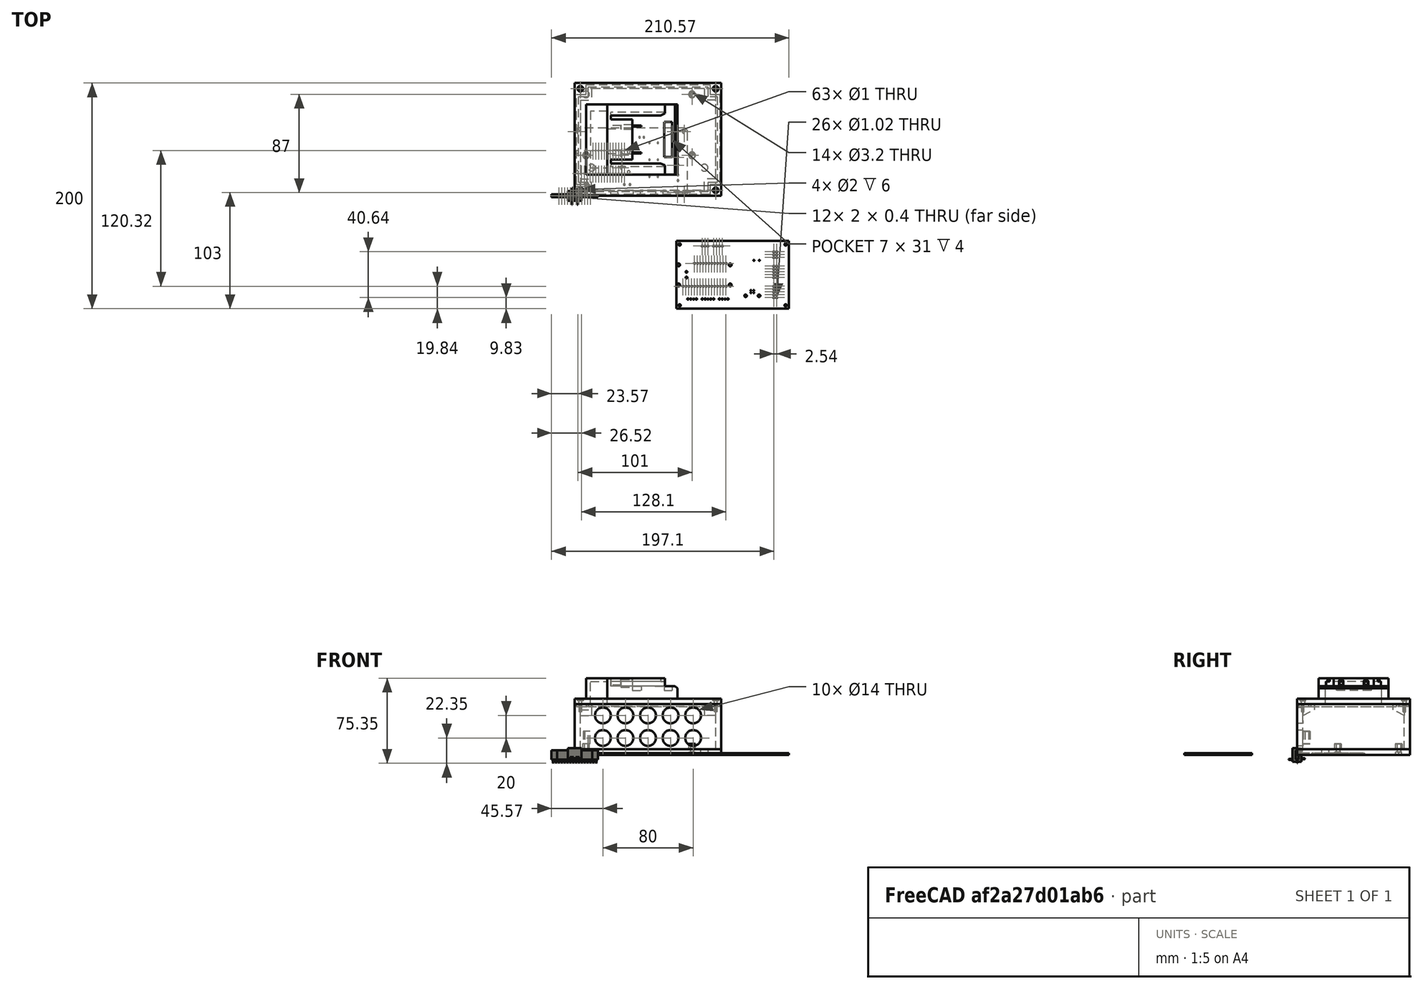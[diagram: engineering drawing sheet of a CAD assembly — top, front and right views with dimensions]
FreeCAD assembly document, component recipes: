
FREECAD ASSEMBLY — COMPONENT RECIPES ("case")

This assembly document has 7 components, labeled P0..P6 below (a component is one placed body or linked part). 5 of them carry a construction recipe — the FreeCAD feature program that regenerates the part from scratch, quoted from this document or its linked companion documents; the rest are supplied as boundary geometry only. No exploded tour is included for this assembly.
COMPONENT P0 — recipe-attached ("middle", modeled in this document).
Construction recipe (the document's own serialized feature program — sketch geometry with constraints, then the solid features built on it; lengths are millimeters unless a unit is written):

FEATURE [Sketcher::SketchObject] Sketch
  MapMode = 5
  Support = -> [XY_Plane]
  sketch-geometry (8):
    g0: LineSegment StartX=0 StartY=0 StartZ=0 EndX=130 EndY=0 EndZ=0
    g1: LineSegment StartX=130 StartY=0 StartZ=0 EndX=130 EndY=100 EndZ=0
    g2: LineSegment StartX=130 StartY=100 StartZ=0 EndX=0 EndY=100 EndZ=0
    g3: LineSegment StartX=0 StartY=100 StartZ=0 EndX=0 EndY=0 EndZ=0
    g4: LineSegment StartX=5 StartY=5 StartZ=0 EndX=125 EndY=5 EndZ=0
    g5: LineSegment StartX=125 StartY=5 StartZ=0 EndX=125 EndY=95 EndZ=0
    g6: LineSegment StartX=125 StartY=95 StartZ=0 EndX=5 EndY=95 EndZ=0
    g7: LineSegment StartX=5 StartY=95 StartZ=0 EndX=5 EndY=5 EndZ=0
  constraints (21):
    c: Coincident(g0,g1)
    c: Coincident(g1,g2)
    c: Coincident(g2,g3)
    c: Coincident(g3,g0)
    c: Horizontal(g0)
    c: Horizontal(g2)
    c: Vertical(g1)
    c: Vertical(g3)
    c: Coincident(g-1,g0)
    c: DistanceX(g2,g2) = 130
    c: DistanceY(g1,g1) = 100
    c: Coincident(g4,g5)
    c: Coincident(g5,g6)
    c: Coincident(g6,g7)
    c: Coincident(g7,g4)
    c: Horizontal(g4)
    c: Horizontal(g6)
    c: Vertical(g5)
    c: Vertical(g7)
    c: DistanceX(g6,g6) = 120
    c: DistanceY(g5,g5) = 90
FEATURE [PartDesign::Pad] Pad
  AllowMultiFace = false
  Length = 40
  Length2 = 100
  Profile = -> Sketch
  Type = 0
FEATURE [Sketcher::SketchObject] Sketch004
  MapMode = 5
  Placement = pos=(5,0,0) rot=(0.57735,0.57735,0.57735;2.0944rad)
  Support = -> [Pad]
  sketch-geometry (8):
    g0: LineSegment StartX=5 StartY=40 StartZ=0 EndX=15 EndY=40 EndZ=0
    g1: LineSegment StartX=15 StartY=40 StartZ=0 EndX=15 EndY=35 EndZ=0
    g2: LineSegment StartX=15 StartY=35 StartZ=0 EndX=5 EndY=35 EndZ=0
    g3: LineSegment StartX=5 StartY=35 StartZ=0 EndX=5 EndY=40 EndZ=0
    g4: LineSegment StartX=85 StartY=40 StartZ=0 EndX=95 EndY=40 EndZ=0
    g5: LineSegment StartX=95 StartY=40 StartZ=0 EndX=95 EndY=35 EndZ=0
    g6: LineSegment StartX=95 StartY=35 StartZ=0 EndX=85 EndY=35 EndZ=0
    g7: LineSegment StartX=85 StartY=35 StartZ=0 EndX=85 EndY=40 EndZ=0
  constraints (21):
    c: Coincident(g0,g1)
    c: Coincident(g1,g2)
    c: Coincident(g2,g3)
    c: Coincident(g3,g0)
    c: Horizontal(g0)
    c: Horizontal(g2)
    c: Vertical(g1)
    c: Vertical(g3)
    c: Coincident(g4,g5)
    c: Coincident(g5,g6)
    c: Coincident(g6,g7)
    c: Coincident(g7,g4)
    c: Horizontal(g4)
    c: Horizontal(g6)
    c: Vertical(g5)
    c: Vertical(g7)
    c: Equal(g4,g0)
    c: Equal(g1,g5)
    c: DistanceY(g3,g3) = 5
    c: DistanceX(g0,g4) = 70
    c: DistanceX(g0,g0) = 10
FEATURE [PartDesign::Pad] Pad003
  AllowMultiFace = false
  BaseFeature = -> Pad
  Length = 10
  Length2 = 100
  Profile = -> Sketch004
  Type = 0
FEATURE [Sketcher::SketchObject] Sketch005
  MapMode = 5
  Placement = pos=(125,0,0) rot=(0.57735,-0.57735,-0.57735;2.0944rad)
  Support = -> [Pad003]
  sketch-geometry (8):
    g0: LineSegment StartX=-95 StartY=40 StartZ=0 EndX=-85 EndY=40 EndZ=0
    g1: LineSegment StartX=-85 StartY=40 StartZ=0 EndX=-85 EndY=35 EndZ=0
    g2: LineSegment StartX=-85 StartY=35 StartZ=0 EndX=-95 EndY=35 EndZ=0
    g3: LineSegment StartX=-95 StartY=35 StartZ=0 EndX=-95 EndY=40 EndZ=0
    g4: LineSegment StartX=-15 StartY=40 StartZ=0 EndX=-5 EndY=40 EndZ=0
    g5: LineSegment StartX=-5 StartY=40 StartZ=0 EndX=-5 EndY=35 EndZ=0
    g6: LineSegment StartX=-5 StartY=35 StartZ=0 EndX=-15 EndY=35 EndZ=0
    g7: LineSegment StartX=-15 StartY=35 StartZ=0 EndX=-15 EndY=40 EndZ=0
  constraints (21):
    c: Coincident(g0,g1)
    c: Coincident(g1,g2)
    c: Coincident(g2,g3)
    c: Coincident(g3,g0)
    c: Horizontal(g0)
    c: Horizontal(g2)
    c: Vertical(g1)
    c: Vertical(g3)
    c: Coincident(g4,g5)
    c: Coincident(g5,g6)
    c: Coincident(g6,g7)
    c: Coincident(g7,g4)
    c: Horizontal(g4)
    c: Horizontal(g6)
    c: Vertical(g5)
    c: Vertical(g7)
    c: Equal(g0,g4)
    c: Equal(g7,g1)
    c: DistanceX(g0,g0) = 10
    c: DistanceY(g1,g1) = 5
    c: DistanceX(g0,g4) = 70
FEATURE [PartDesign::Pad] Pad004
  AllowMultiFace = false
  BaseFeature = -> Pad003
  Length = 10
  Length2 = 100
  Profile = -> Sketch005
  Type = 0
FEATURE [Sketcher::SketchObject] Sketch006
  MapMode = 5
  Placement = pos=(5,0,0) rot=(0.57735,0.57735,0.57735;2.0944rad)
  Support = -> [Pad004]
  sketch-geometry (6):
    g0: LineSegment StartX=5 StartY=30 StartZ=0 EndX=5 EndY=35 EndZ=0
    g1: LineSegment StartX=5 StartY=35 StartZ=0 EndX=15 EndY=35 EndZ=0
    g2: LineSegment StartX=85 StartY=35 StartZ=0 EndX=95 EndY=35 EndZ=0
    g3: LineSegment StartX=95 StartY=35 StartZ=0 EndX=95 EndY=30 EndZ=0
    g4: LineSegment StartX=95 StartY=30 StartZ=0 EndX=85 EndY=35 EndZ=0
    g5: LineSegment StartX=5 StartY=30 StartZ=0 EndX=15 EndY=35 EndZ=0
  constraints (13):
    c: Coincident(g0,g1)
    c: Coincident(g2,g3)
    c: Coincident(g3,g4)
    c: Horizontal(g2)
    c: Horizontal(g1)
    c: Vertical(g0)
    c: Vertical(g3)
    c: Coincident(g5,g1)
    c: Equal(g2,g1)
    c: Equal(g0,g3)
    c: DistanceX(g1,g1) = 10
    c: DistanceX(g1,g2) = 70
    c: DistanceY(g0,g0) = 5
FEATURE [PartDesign::Pad] Pad005
  AllowMultiFace = false
  BaseFeature = -> Pad004
  Length = 10
  Length2 = 100
  Profile = -> Sketch006
  Type = 0
FEATURE [Sketcher::SketchObject] Sketch007
  MapMode = 5
  Placement = pos=(125,0,0) rot=(0.57735,-0.57735,-0.57735;2.0944rad)
  Support = -> [Pad005]
  sketch-geometry (7):
    g0: LineSegment StartX=0 StartY=35 StartZ=0 EndX=-5 EndY=35 EndZ=0
    g1: LineSegment StartX=-5 StartY=35 StartZ=0 EndX=-5 EndY=30 EndZ=0
    g2: LineSegment StartX=-5 StartY=30 StartZ=0 EndX=-15 EndY=35 EndZ=0
    g3: LineSegment StartX=-85 StartY=35 StartZ=0 EndX=-95 EndY=35 EndZ=0
    g4: LineSegment StartX=-95 StartY=35 StartZ=0 EndX=-95 EndY=30 EndZ=0
    g5: LineSegment StartX=-95 StartY=30 StartZ=0 EndX=-85 EndY=35 EndZ=0
    g6: LineSegment StartX=-15 StartY=35 StartZ=0 EndX=-5 EndY=35 EndZ=0
  constraints (18):
    c: Coincident(g0,g1)
    c: Coincident(g1,g2)
    c: Coincident(g3,g4)
    c: Coincident(g4,g5)
    c: Coincident(g6,g0)
    c: Coincident(g2,g6)
    c: Vertical(g1)
    c: Vertical(g4)
    c: Horizontal(g6)
    c: Horizontal(g3)
    c: Horizontal(g0)
    c: Equal(g6,g3)
    c: Equal(g4,g1)
    c: DistanceY(g-1,g0) = 35
    c: DistanceY(g1,g1) = 5
    c: DistanceX(g0,g0) = 5
    c: DistanceX(g6,g6) = 10
    c: DistanceX(g3,g2) = 70
FEATURE [PartDesign::Pad] Pad006
  AllowMultiFace = false
  BaseFeature = -> Pad005
  Length = 10
  Length2 = 100
  Profile = -> Sketch007
  Type = 0
FEATURE [Sketcher::SketchObject] Sketch009
  MapMode = 5
  Placement = pos=(0,0,40) rot=(0,0,1;0rad)
  sketch-geometry (4):
    g0: Circle CenterX=5 CenterY=95 CenterZ=0 NormalX=0 NormalY=0 NormalZ=1 AngleXU=0 Radius=1
    g1: Circle CenterX=125 CenterY=95 CenterZ=0 NormalX=0 NormalY=0 NormalZ=1 AngleXU=0 Radius=1
    g2: Circle CenterX=125 CenterY=5 CenterZ=0 NormalX=0 NormalY=0 NormalZ=1 AngleXU=0 Radius=1
    g3: Circle CenterX=5 CenterY=5 CenterZ=0 NormalX=0 NormalY=0 NormalZ=1 AngleXU=0 Radius=1
  constraints (6):
    c: DistanceY(g3,g0) = 90
    c: DistanceX(g0,g1) = 120
    c: Equal(g0,g1)
    c: Equal(g0,g2)
    c: Equal(g0,g3)
    c: Radius(g0) = 1
FEATURE [PartDesign::Pocket] Pocket002
  AllowMultiFace = false
  BaseFeature = -> Pad006
  Length = 7
  Length2 = 100
  Profile = -> Sketch009
  Type = 0
FEATURE [Sketcher::SketchObject] Sketch011
  MapMode = 5
  Placement = pos=(0,0,0) rot=(1,0,0;1.5708rad)
  sketch-geometry (10):
    g0: Circle CenterX=25 CenterY=30 CenterZ=0 NormalX=0 NormalY=0 NormalZ=1 AngleXU=0 Radius=7
    g1: Circle CenterX=45 CenterY=30 CenterZ=0 NormalX=0 NormalY=0 NormalZ=1 AngleXU=0 Radius=7
    g2: Circle CenterX=45 CenterY=10 CenterZ=0 NormalX=0 NormalY=0 NormalZ=1 AngleXU=0 Radius=7
    g3: Circle CenterX=25 CenterY=10 CenterZ=0 NormalX=0 NormalY=0 NormalZ=1 AngleXU=0 Radius=7
    g4: Circle CenterX=65 CenterY=30 CenterZ=0 NormalX=0 NormalY=0 NormalZ=1 AngleXU=0 Radius=7
    g5: Circle CenterX=85 CenterY=30 CenterZ=0 NormalX=0 NormalY=0 NormalZ=1 AngleXU=0 Radius=7
    g6: Circle CenterX=85 CenterY=10 CenterZ=0 NormalX=0 NormalY=0 NormalZ=1 AngleXU=0 Radius=7
    g7: Circle CenterX=65 CenterY=10 CenterZ=0 NormalX=0 NormalY=0 NormalZ=1 AngleXU=0 Radius=7
    g8: Circle CenterX=105 CenterY=10 CenterZ=0 NormalX=0 NormalY=0 NormalZ=1 AngleXU=0 Radius=7
    g9: Circle CenterX=105 CenterY=30 CenterZ=0 NormalX=0 NormalY=0 NormalZ=1 AngleXU=0 Radius=7
  constraints (12):
    c: Equal(g0,g1)
    c: Equal(g1,g2)
    c: Equal(g2,g3)
    c: Equal(g4,g5)
    c: Equal(g3,g7)
    c: Equal(g2,g6)
    c: Equal(g1,g5)
    c: Radius(g0) = 7
    c: DistanceX(g0,g1) = 20
    c: DistanceY(g6,g5) = 20
    c: Equal(g6,g8)
    c: Equal(g9,g8)
FEATURE [PartDesign::Pocket] Pocket004
  AllowMultiFace = false
  BaseFeature = -> Pocket002
  Length = 5
  Length2 = 100
  Profile = -> Sketch011
  Type = 0
FEATURE [PartDesign::Pocket] Pocket007
  AllowMultiFace = false
  BaseFeature = -> Pocket004
  Length = 1
  Length2 = 100
  Profile = -> Sketch009
  Type = 0
FEATURE [Sketcher::SketchObject] Sketch014
  MapMode = 5
  Placement = pos=(0,0,40) rot=(0,0,1;0rad)
  Support = -> [Pocket004]
  sketch-geometry (25):
    g0: LineSegment StartX=12 StartY=88 StartZ=0 EndX=12 EndY=96.5 EndZ=0
    g1: LineSegment StartX=12 StartY=96.5 StartZ=0 EndX=118 EndY=96.5 EndZ=0
    g2: LineSegment StartX=118 StartY=96.5 StartZ=0 EndX=118 EndY=88 EndZ=0
    g3: LineSegment StartX=118 StartY=88 StartZ=0 EndX=126.5 EndY=88 EndZ=0
    g4: LineSegment StartX=126.5 StartY=88 StartZ=0 EndX=126.5 EndY=12 EndZ=0
    g5: LineSegment StartX=126.5 StartY=12 StartZ=0 EndX=118 EndY=12 EndZ=0
    g6: LineSegment StartX=118 StartY=12 StartZ=0 EndX=118 EndY=3.5 EndZ=0
    g7: LineSegment StartX=118 StartY=3.5 StartZ=0 EndX=12 EndY=3.5 EndZ=0
    g8: LineSegment StartX=12 StartY=3.5 StartZ=0 EndX=12 EndY=12 EndZ=0
    g9: LineSegment StartX=12 StartY=12 StartZ=0 EndX=3.5 EndY=12 EndZ=0
    g10: LineSegment StartX=3.5 StartY=12 StartZ=0 EndX=3.5 EndY=88 EndZ=0
    g11: LineSegment StartX=3.5 StartY=88 StartZ=0 EndX=12 EndY=88 EndZ=0
    g12: LineSegment StartX=1.5 StartY=10 StartZ=0 EndX=1.5 EndY=90 EndZ=0
    g13: LineSegment StartX=1.5 StartY=90 StartZ=0 EndX=10 EndY=90 EndZ=0
    g14: LineSegment StartX=10 StartY=90 StartZ=0 EndX=10 EndY=98.5 EndZ=0
    g15: LineSegment StartX=10 StartY=98.5 StartZ=0 EndX=120 EndY=98.5 EndZ=0
    g16: LineSegment StartX=120 StartY=98.5 StartZ=0 EndX=120 EndY=90 EndZ=0
    g17: LineSegment StartX=120 StartY=90 StartZ=0 EndX=128.5 EndY=90 EndZ=0
    g18: LineSegment StartX=128.5 StartY=90 StartZ=0 EndX=128.5 EndY=10 EndZ=0
    g19: LineSegment StartX=128.5 StartY=10 StartZ=0 EndX=120 EndY=10 EndZ=0
    g20: LineSegment StartX=120 StartY=10 StartZ=0 EndX=120 EndY=1.5 EndZ=0
    g21: LineSegment StartX=120 StartY=1.5 StartZ=0 EndX=10 EndY=1.5 EndZ=0
    g22: LineSegment StartX=10 StartY=1.5 StartZ=0 EndX=10 EndY=10 EndZ=0
    g23: LineSegment StartX=10 StartY=10 StartZ=0 EndX=1.5 EndY=10 EndZ=0
    g24: LineSegment StartX=120 StartY=88 StartZ=0 EndX=118 EndY=88 EndZ=0
  constraints (72):
    c: Coincident(g0,g1)
    c: Coincident(g1,g2)
    c: Coincident(g2,g3)
    c: Coincident(g3,g4)
    c: Coincident(g4,g5)
    c: Coincident(g5,g6)
    c: Coincident(g6,g7)
    c: Coincident(g7,g8)
    c: Coincident(g8,g9)
    c: Coincident(g9,g10)
    c: Coincident(g10,g11)
    c: Coincident(g11,g0)
    c: Vertical(g0)
    c: Vertical(g10)
    c: Vertical(g8)
    c: Vertical(g6)
    c: Vertical(g4)
    c: Horizontal(g1)
    c: Horizontal(g3)
    c: Horizontal(g5)
    c: Horizontal(g7)
    c: Horizontal(g9)
    c: Equal(g1,g7)
    c: Equal(g10,g4)
    c: Equal(g5,g6)
    c: Equal(g3,g2)
    c: Equal(g3,g5)
    c: Equal(g9,g8)
    c: Equal(g0,g11)
    c: Equal(g11,g9)
    c: Equal(g2,g0)
    c: Coincident(g12,g13)
    c: Coincident(g13,g14)
    c: Coincident(g14,g15)
    c: Coincident(g15,g16)
    c: Coincident(g16,g17)
    c: Coincident(g17,g18)
    c: Coincident(g18,g19)
    c: Coincident(g19,g20)
    c: Coincident(g20,g21)
    c: Coincident(g21,g22)
    c: Coincident(g22,g23)
    c: Coincident(g23,g12)
    c: Horizontal(g15)
    c: Horizontal(g21)
    c: Horizontal(g19)
    c: Horizontal(g17)
    c: Horizontal(g13)
    c: Vertical(g12)
    c: Vertical(g22)
    c: Vertical(g20)
    c: Vertical(g18)
    c: Vertical(g16)
    c: Equal(g15,g21)
    c: Equal(g18,g12)
    c: Equal(g22,g20)
    c: Equal(g19,g23)
    c: Equal(g20,g19)
    c: Equal(g17,g16)
    c: Equal(g17,g19)
    c: Equal(g14,g13)
    c: Equal(g14,g16)
    c: Equal(g22,g19)
    c: DistanceY(g12,g12) = 80
    c: DistanceX(g13,g13) = 8.5
    c: DistanceX(g21,g21) = 110
    c: Horizontal(g24)
    c: DistanceY(g24,g16) = 2
    c: DistanceX(g24,g24) = 2
    c: Coincident(g2,g24)
    c: DistanceX(g7,g7) = 106
    c: DistanceY(g4,g4) = 76
FEATURE [PartDesign::Pocket] Pocket008
  AllowMultiFace = false
  BaseFeature = -> Pocket007
  Length = 2
  Length2 = 100
  Profile = -> Sketch014
  Type = 0
FEATURE [PartDesign::Body] Body  label="middle"
  Group = -> [Sketch,Pad,Sketch004,Pad003,Sketch005,Pad004,Sketch006,Pad005,Sketch007,Pad006,Sketch009,Pocket002,Sketch011,Pocket004,Pocket007,Sketch014,Pocket008]
  Origin = -> Origin
  Placement = pos=(0,0,5) rot=(0,0,1;0rad)
  Tip = -> Pocket008
COMPONENT P1 — recipe-attached ("bottom", modeled in this document).
Construction recipe (the document's own serialized feature program — sketch geometry with constraints, then the solid features built on it; lengths are millimeters unless a unit is written):

FEATURE [Sketcher::SketchObject] Sketch001
  MapMode = 5
  Support = -> [XY_Plane001]
  sketch-geometry (4):
    g0: LineSegment StartX=0 StartY=0 StartZ=0 EndX=130 EndY=0 EndZ=0
    g1: LineSegment StartX=130 StartY=0 StartZ=0 EndX=130 EndY=100 EndZ=0
    g2: LineSegment StartX=130 StartY=100 StartZ=0 EndX=0 EndY=100 EndZ=0
    g3: LineSegment StartX=0 StartY=100 StartZ=0 EndX=0 EndY=0 EndZ=0
  constraints (11):
    c: Coincident(g0,g1)
    c: Coincident(g1,g2)
    c: Coincident(g2,g3)
    c: Coincident(g3,g0)
    c: Horizontal(g0)
    c: Horizontal(g2)
    c: Vertical(g1)
    c: Vertical(g3)
    c: DistanceX(g2,g2) = 130
    c: DistanceY(g1,g1) = 100
    c: Coincident(g-1,g0)
FEATURE [PartDesign::Pad] Pad001
  AllowMultiFace = false
  Length = 5
  Length2 = 100
  Profile = -> Sketch001
  Type = 0
FEATURE [Sketcher::SketchObject] Sketch002
  MapMode = 5
  Placement = pos=(0,0,5) rot=(0,0,1;0rad)
  Support = -> [Pad001]
  sketch-geometry (4):
    g0: Circle CenterX=10 CenterY=90 CenterZ=0 NormalX=0 NormalY=0 NormalZ=1 AngleXU=0 Radius=3
    g1: Circle CenterX=10 CenterY=36 CenterZ=0 NormalX=0 NormalY=0 NormalZ=1 AngleXU=0 Radius=3
    g2: Circle CenterX=104 CenterY=90 CenterZ=0 NormalX=0 NormalY=0 NormalZ=1 AngleXU=0 Radius=3
    g3: Circle CenterX=104 CenterY=36 CenterZ=0 NormalX=0 NormalY=0 NormalZ=1 AngleXU=0 Radius=3
  constraints (6):
    c: DistanceX(g0,g2) = 94
    c: DistanceY(g3,g2) = 54
    c: Equal(g1,g0)
    c: Equal(g2,g1)
    c: Equal(g3,g2)
    c: Radius(g0) = 3
FEATURE [PartDesign::Pad] Pad002
  AllowMultiFace = false
  BaseFeature = -> Pad001
  Length = 5
  Length2 = 100
  Profile = -> Sketch002
  Type = 0
FEATURE [Sketcher::SketchObject] Sketch003
  MapMode = 5
  Placement = pos=(0,0,0) rot=(1,0,0;3.14159rad)
  Support = -> [Pad002]
  sketch-geometry (3):
    g0: Circle CenterX=10 CenterY=-36 CenterZ=0 NormalX=0 NormalY=0 NormalZ=1 AngleXU=0 Radius=1.6
    g1: Circle CenterX=104 CenterY=-36 CenterZ=0 NormalX=0 NormalY=0 NormalZ=1 AngleXU=0 Radius=1.6
    g2: Circle CenterX=104 CenterY=-90 CenterZ=0 NormalX=0 NormalY=0 NormalZ=1 AngleXU=0 Radius=1.6
  constraints (3):
    c: DistanceY(g2,g1) = 54
    c: Equal(g0,g1)
    c: Radius(g0) = 1.6
FEATURE [PartDesign::Pocket] Pocket
  AllowMultiFace = false
  BaseFeature = -> Pad002
  Length = 10
  Length2 = 100
  Profile = -> Sketch003
  Type = 0
FEATURE [Sketcher::SketchObject] Sketch012
  MapMode = 5
  Placement = pos=(0,0,0) rot=(1,0,0;3.14159rad)
  Support = -> [Pocket]
  sketch-geometry (21):
    g0: LineSegment StartX=107.1 StartY=-90 StartZ=0 EndX=105.55 EndY=-87.3153 EndZ=0
    g1: LineSegment StartX=105.55 StartY=-87.3153 StartZ=0 EndX=102.45 EndY=-87.3153 EndZ=0
    g2: LineSegment StartX=102.45 StartY=-87.3153 StartZ=0 EndX=100.9 EndY=-90 EndZ=0
    g3: LineSegment StartX=100.9 StartY=-90 StartZ=0 EndX=102.45 EndY=-92.6847 EndZ=0
    g4: LineSegment StartX=102.45 StartY=-92.6847 StartZ=0 EndX=105.55 EndY=-92.6847 EndZ=0
    g5: LineSegment StartX=105.55 StartY=-92.6847 StartZ=0 EndX=107.1 EndY=-90 EndZ=0
    g6: Circle [constr] CenterX=104 CenterY=-90 CenterZ=0 NormalX=0 NormalY=0 NormalZ=1 AngleXU=0 Radius=3.1
    g7: LineSegment StartX=13.1 StartY=-36 StartZ=0 EndX=11.55 EndY=-33.3153 EndZ=0
    g8: LineSegment StartX=11.55 StartY=-33.3153 StartZ=0 EndX=8.45 EndY=-33.3153 EndZ=0
    g9: LineSegment StartX=8.45 StartY=-33.3153 StartZ=0 EndX=6.9 EndY=-36 EndZ=0
    g10: LineSegment StartX=6.9 StartY=-36 StartZ=0 EndX=8.45 EndY=-38.6847 EndZ=0
    g11: LineSegment StartX=8.45 StartY=-38.6847 StartZ=0 EndX=11.55 EndY=-38.6847 EndZ=0
    g12: LineSegment StartX=11.55 StartY=-38.6847 StartZ=0 EndX=13.1 EndY=-36 EndZ=0
    g13: Circle [constr] CenterX=10 CenterY=-36 CenterZ=0 NormalX=0 NormalY=0 NormalZ=1 AngleXU=0 Radius=3.1
    g14: LineSegment StartX=107.1 StartY=-36 StartZ=0 EndX=105.55 EndY=-33.3153 EndZ=0
    g15: LineSegment StartX=105.55 StartY=-33.3153 StartZ=0 EndX=102.45 EndY=-33.3153 EndZ=0
    g16: LineSegment StartX=102.45 StartY=-33.3153 StartZ=0 EndX=100.9 EndY=-36 EndZ=0
    g17: LineSegment StartX=100.9 StartY=-36 StartZ=0 EndX=102.45 EndY=-38.6847 EndZ=0
    g18: LineSegment StartX=102.45 StartY=-38.6847 StartZ=0 EndX=105.55 EndY=-38.6847 EndZ=0
    g19: LineSegment StartX=105.55 StartY=-38.6847 StartZ=0 EndX=107.1 EndY=-36 EndZ=0
    g20: Circle [constr] CenterX=104 CenterY=-36 CenterZ=0 NormalX=0 NormalY=0 NormalZ=1 AngleXU=0 Radius=3.1
  constraints (45):
    c: Coincident(g0,g1)
    c: Coincident(g1,g2)
    c: Coincident(g2,g3)
    c: Coincident(g3,g4)
    c: Coincident(g4,g5)
    c: Coincident(g5,g0)
    c: Equal(g0, g1-g5) x5
    c: PointOnObject(g0,g6)
    c: PointOnObject(g1,g6)
    c: PointOnObject(g2,g6)
    c: PointOnObject(g3,g6)
    c: PointOnObject(g4,g6)
    c: PointOnObject(g5,g6)
    c: Horizontal(g1)
    c: DistanceX(g1,g1) = 3.1
    c: Coincident(g7,g8)
    c: Coincident(g8,g9)
    c: Coincident(g9,g10)
    c: Coincident(g10,g11)
    c: Coincident(g11,g12)
    c: Coincident(g12,g7)
    c: Equal(g7, g8-g12) x5
    c: PointOnObject(g7,g13)
    c: PointOnObject(g8,g13)
    c: PointOnObject(g9,g13)
    c: PointOnObject(g10,g13)
    c: PointOnObject(g11,g13)
    c: PointOnObject(g12,g13)
    c: Horizontal(g8)
    c: Equal(g1,g8) = 3.1
    c: Coincident(g14,g15)
    c: Coincident(g15,g16)
    c: Coincident(g16,g17)
    c: Coincident(g17,g18)
    c: Coincident(g18,g19)
    c: Coincident(g19,g14)
    c: Equal(g14, g15-g19) x5
    c: PointOnObject(g14,g20)
    c: PointOnObject(g15,g20)
    c: PointOnObject(g16,g20)
    c: PointOnObject(g17,g20)
    c: PointOnObject(g18,g20)
    c: PointOnObject(g19,g20)
    c: Horizontal(g15)
    c: Equal(g1,g15) = 3.1
FEATURE [PartDesign::Pocket] Pocket005
  AllowMultiFace = false
  BaseFeature = -> Pocket
  Length = 2.5
  Length2 = 100
  Profile = -> Sketch012
  Type = 0
FEATURE [Sketcher::SketchObject] Sketch013
  MapMode = 5
  Placement = pos=(0,0,5) rot=(0,0,1;0rad)
  Support = -> [Pad001]
  sketch-geometry (2):
    g0: Circle CenterX=115 CenterY=25 CenterZ=0 NormalX=0 NormalY=0 NormalZ=1 AngleXU=0 Radius=3.1
    g1: Circle CenterX=15 CenterY=25 CenterZ=0 NormalX=0 NormalY=0 NormalZ=1 AngleXU=0 Radius=3.1
  constraints (3):
    c: DistanceX(g1,g0) = 100
    c: Equal(g0,g1)
    c: Radius(g0) = 3.1
FEATURE [PartDesign::Pocket] Pocket006
  AllowMultiFace = false
  BaseFeature = -> Pocket005
  Length = 5
  Length2 = 100
  Profile = -> Sketch013
  Type = 0
FEATURE [PartDesign::Body] Body001  label="bottom"
  Group = -> [Sketch001,Pad001,Sketch002,Pad002,Sketch003,Pocket,Sketch012,Pocket005,Sketch013,Pocket006]
  Origin = -> Origin001
  Tip = -> Pocket006
COMPONENT P2 — recipe-attached ("battery_adapter_einhell_x-change", modeled in this document).
Construction recipe (the document's own serialized feature program — sketch geometry with constraints, then the solid features built on it; lengths are millimeters unless a unit is written):

FEATURE [Sketcher::SketchObject] Sketch072
  MapMode = 5
  Support = -> [XY_Plane122]
  sketch-geometry (4):
    g0: LineSegment StartX=-31 StartY=-31 StartZ=0 EndX=-31 EndY=31 EndZ=0
    g1: LineSegment StartX=-31 StartY=31 StartZ=0 EndX=31 EndY=31 EndZ=0
    g2: LineSegment StartX=31 StartY=31 StartZ=0 EndX=31 EndY=-31 EndZ=0
    g3: LineSegment StartX=31 StartY=-31 StartZ=0 EndX=-31 EndY=-31 EndZ=0
  constraints (9):
    c: Coincident(g0,g1)
    c: Coincident(g1,g2)
    c: Coincident(g2,g3)
    c: Coincident(g0,g3)
    c: Symmetric(g0,g0,g-1)
    c: Symmetric(g1,g2,g-1)
    c: Symmetric(g1,g0,g-2)
    c: DistanceX(g0,g1) = 62
    c: DistanceY(g2,g1) = 62
FEATURE [PartDesign::Pad] Pad012
  AllowMultiFace = false
  Length = 18
  Length2 = 100
  Profile = -> Sketch072
  Type = 0
FEATURE [Sketcher::SketchObject] Sketch074
  MapMode = 5
  Placement = pos=(0,-31,0) rot=(1,0,0;1.5708rad)
  sketch-geometry (12):
    g0: LineSegment StartX=-21.25 StartY=20 StartZ=0 EndX=-21.25 EndY=15 EndZ=0
    g1: LineSegment StartX=-21.25 StartY=15 StartZ=0 EndX=-24.25 EndY=15 EndZ=0
    g2: LineSegment StartX=-24.25 StartY=15 StartZ=0 EndX=-24.25 EndY=11 EndZ=0
    g3: LineSegment StartX=-24.25 StartY=11 StartZ=0 EndX=-17.75 EndY=11 EndZ=0
    g4: LineSegment StartX=-17.75 StartY=11 StartZ=0 EndX=-17.75 EndY=18 EndZ=0
    g5: LineSegment StartX=-17.75 StartY=18 StartZ=0 EndX=17.75 EndY=18 EndZ=0
    g6: LineSegment StartX=17.75 StartY=18 StartZ=0 EndX=17.75 EndY=11 EndZ=0
    g7: LineSegment StartX=17.75 StartY=11 StartZ=0 EndX=24.25 EndY=11 EndZ=0
    g8: LineSegment StartX=24.25 StartY=11 StartZ=0 EndX=24.25 EndY=15 EndZ=0
    g9: LineSegment StartX=24.25 StartY=15 StartZ=0 EndX=21.25 EndY=15 EndZ=0
    g10: LineSegment StartX=21.25 StartY=15 StartZ=0 EndX=21.25 EndY=20 EndZ=0
    g11: LineSegment StartX=21.25 StartY=20 StartZ=0 EndX=-21.25 EndY=20 EndZ=0
  constraints (32):
    c: Vertical(g0)
    c: Coincident(g0,g1)
    c: Coincident(g1,g2)
    c: Vertical(g2)
    c: Coincident(g2,g3)
    c: Horizontal(g3)
    c: Coincident(g3,g4)
    c: Vertical(g4)
    c: Coincident(g4,g5)
    c: Coincident(g5,g6)
    c: Coincident(g6,g7)
    c: Coincident(g7,g8)
    c: Coincident(g8,g9)
    c: Coincident(g9,g10)
    c: Coincident(g10,g11)
    c: Horizontal(g11)
    c: Coincident(g11,g0)
    c: Horizontal(g1)
    c: Horizontal(g9)
    c: Vertical(g10)
    c: DistanceX(g2,g3) = 6.5
    c: DistanceX(g9,g8) = 3
    c: DistanceX(g1,g0) = 3
    c: DistanceX(g4,g5) = 35.5
    c: Symmetric(g4,g5,g-2)
    c: DistanceY(g-1,g5) = 18
    c: DistanceY(g7,g8) = 4
    c: DistanceY(g6,g5) = 7
    c: DistanceY(g9,g10) = 5
    c: Symmetric(g3,g6,g-2)
    c: Symmetric(g2,g7,g-2)
    c: Symmetric(g8,g1,g-2)
FEATURE [PartDesign::Pocket] Pocket059
  AllowMultiFace = false
  BaseFeature = -> Pad012
  Length = 59
  Length2 = 100
  Profile = -> Sketch074
  Type = 0
FEATURE [Sketcher::SketchObject] Sketch075
  MapMode = 5
  Placement = pos=(0,0,18) rot=(0,0,1;0rad)
  Support = -> [Pocket059]
  sketch-geometry (10):
    g0: LineSegment StartX=-19 StartY=-11 StartZ=0 EndX=-19 EndY=9 EndZ=0
    g1: LineSegment StartX=-19 StartY=9 StartZ=0 EndX=19 EndY=9 EndZ=0
    g2: LineSegment StartX=19 StartY=9 StartZ=0 EndX=19 EndY=-11 EndZ=0
    g3: LineSegment StartX=31 StartY=-31 StartZ=0 EndX=-31 EndY=-31 EndZ=0
    g4: LineSegment StartX=-19 StartY=-11 StartZ=0 EndX=-23 EndY=-20 EndZ=0
    g5: LineSegment StartX=-23 StartY=-20 StartZ=0 EndX=-31 EndY=-20 EndZ=0
    g6: LineSegment StartX=-31 StartY=-20 StartZ=0 EndX=-31 EndY=-31 EndZ=0
    g7: LineSegment StartX=19 StartY=-11 StartZ=0 EndX=23 EndY=-20 EndZ=0
    g8: LineSegment StartX=23 StartY=-20 StartZ=0 EndX=31 EndY=-20 EndZ=0
    g9: LineSegment StartX=31 StartY=-20 StartZ=0 EndX=31 EndY=-31 EndZ=0
  constraints (25):
    c: Coincident(g0,g1)
    c: Coincident(g1,g2)
    c: Vertical(g2)
    c: Symmetric(g0,g1,g-2)
    c: Symmetric(g0,g2,g-2)
    c: Symmetric(g3,g3,g-2)
    c: DistanceX(g0,g1) = 38
    c: DistanceX(g3,g3) = 62
    c: DistanceY(g3,g2) = 20
    c: DistanceY(g-1,g1) = 9
    c: DistanceY(g3,g-1) = 31
    c: Coincident(g4,g5)
    c: Coincident(g5,g6)
    c: Coincident(g7,g8)
    c: Coincident(g8,g9)
    c: Coincident(g4,g0)
    c: Coincident(g7,g2)
    c: Coincident(g6,g3)
    c: Coincident(g9,g3)
    c: Horizontal(g8)
    c: Vertical(g9)
    c: Symmetric(g8,g5,g-2)
    c: Symmetric(g4,g7,g-2)
    c: DistanceY(g3,g8) = 11
    c: DistanceX(g7,g8) = 8
FEATURE [PartDesign::Pocket] Pocket060
  AllowMultiFace = false
  BaseFeature = -> Pocket059
  Length = 7
  Length2 = 100
  Profile = -> Sketch075
  Type = 0
FEATURE [Sketcher::SketchObject] Sketch076
  MapMode = 5
  Placement = pos=(0,0,18) rot=(0,0,1;0rad)
  Support = -> [Pocket060]
  sketch-geometry (12):
    g0: LineSegment StartX=-15.5 StartY=-19.5 StartZ=0 EndX=15.5 EndY=-19.5 EndZ=0
    g1: LineSegment StartX=15.5 StartY=-19.5 StartZ=0 EndX=15.5 EndY=-26.5 EndZ=0
    g2: LineSegment StartX=15.5 StartY=-26.5 StartZ=0 EndX=-15.5 EndY=-26.5 EndZ=0
    g3: LineSegment StartX=-15.5 StartY=-26.5 StartZ=0 EndX=-15.5 EndY=-19.5 EndZ=0
    g4: LineSegment StartX=-12.5 StartY=9 StartZ=0 EndX=-11.5 EndY=9 EndZ=0
    g5: LineSegment StartX=-11.5 StartY=9 StartZ=0 EndX=-11.5 EndY=1 EndZ=0
    g6: LineSegment StartX=-11.5 StartY=1 StartZ=0 EndX=-12.5 EndY=1 EndZ=0
    g7: LineSegment StartX=-12.5 StartY=1 StartZ=0 EndX=-12.5 EndY=9 EndZ=0
    g8: LineSegment StartX=11.5 StartY=9 StartZ=0 EndX=12.5 EndY=9 EndZ=0
    g9: LineSegment StartX=12.5 StartY=9 StartZ=0 EndX=12.5 EndY=1 EndZ=0
    g10: LineSegment StartX=12.5 StartY=1 StartZ=0 EndX=11.5 EndY=1 EndZ=0
    g11: LineSegment StartX=11.5 StartY=1 StartZ=0 EndX=11.5 EndY=9 EndZ=0
  constraints (30):
    c: Coincident(g0,g1)
    c: Coincident(g1,g2)
    c: Coincident(g2,g3)
    c: Coincident(g3,g0)
    c: Symmetric(g0,g0,g-2)
    c: Symmetric(g1,g2,g-2)
    c: Vertical(g1)
    c: DistanceX(g0,g0) = 31
    c: DistanceY(g1,g0) = 7
    c: DistanceY(g1,g-1) = 26.5
    c: Coincident(g4,g5)
    c: Coincident(g5,g6)
    c: Coincident(g6,g7)
    c: Coincident(g7,g4)
    c: Horizontal(g4)
    c: Horizontal(g6)
    c: Vertical(g5)
    c: Vertical(g7)
    c: Coincident(g8,g9)
    c: Coincident(g9,g10)
    c: Coincident(g10,g11)
    c: Coincident(g11,g8)
    c: Symmetric(g4,g8,g-2)
    c: Symmetric(g4,g8,g-2)
    c: Symmetric(g5,g10,g-2)
    c: Symmetric(g6,g9,g-2)
    c: DistanceY(g6,g4) = 8
    c: DistanceY(g-1,g4) = 9
    c: DistanceX(g4,g4) = 1
    c: DistanceX(g4,g8) = 23
FEATURE [Sketcher::SketchObject] Sketch077
  MapMode = 5
  Placement = pos=(0,31,0) rot=(0,0.707107,0.707107;3.14159rad)
  sketch-geometry (2):
    g0: Circle CenterX=-11 CenterY=13.5 CenterZ=0 NormalX=0 NormalY=0 NormalZ=1 AngleXU=0 Radius=1.5
    g1: Circle CenterX=11 CenterY=13.5 CenterZ=0 NormalX=0 NormalY=0 NormalZ=1 AngleXU=0 Radius=1.5
  constraints (5):
    c: Symmetric(g0,g1,g-2)
    c: DistanceX(g0,g1) = 22
    c: Diameter(g1) = 3
    c: Equal(g0,g1)
    c: DistanceY(g-1,g1) = 13.5
FEATURE [PartDesign::Pocket] Pocket062
  AllowMultiFace = false
  BaseFeature = -> Pocket060
  Length = 22
  Length2 = 100
  Profile = -> Sketch077
  Type = 0
FEATURE [Sketcher::SketchObject] Sketch081
  MapMode = 5
  Placement = pos=(0,9,0) rot=(1,0,0;1.5708rad)
  Support = -> [Pocket062]
  sketch-geometry (8):
    g0: ArcOfCircle CenterX=-11 CenterY=15 CenterZ=0 NormalX=0 NormalY=0 NormalZ=1 AngleXU=0 Radius=2 StartAngle=5e-16 EndAngle=3.14159
    g1: ArcOfCircle CenterX=-11 CenterY=12 CenterZ=0 NormalX=0 NormalY=0 NormalZ=1 AngleXU=0 Radius=2 StartAngle=3.14159 EndAngle=6.28319
    g2: LineSegment StartX=-13 StartY=15 StartZ=0 EndX=-13 EndY=12 EndZ=0
    g3: LineSegment StartX=-9 StartY=15 StartZ=0 EndX=-9 EndY=12 EndZ=0
    g4: ArcOfCircle CenterX=11 CenterY=15 CenterZ=0 NormalX=0 NormalY=0 NormalZ=1 AngleXU=0 Radius=2 StartAngle=0 EndAngle=3.14159
    g5: ArcOfCircle CenterX=11 CenterY=12 CenterZ=0 NormalX=0 NormalY=0 NormalZ=1 AngleXU=0 Radius=2 StartAngle=3.14159 EndAngle=6.28319
    g6: LineSegment StartX=9 StartY=15 StartZ=0 EndX=9 EndY=12 EndZ=0
    g7: LineSegment StartX=13 StartY=15 StartZ=0 EndX=13 EndY=12 EndZ=0
  constraints (18):
    c: Tangent(g0,g3) = 1.5708
    c: Tangent(g0,g2) = -1.5708
    c: Tangent(g2,g1) = -1.5708
    c: Tangent(g3,g1) = 1.5708
    c: Vertical(g2)
    c: Equal(g0,g1)
    c: Tangent(g4,g7) = 1.5708
    c: Tangent(g4,g6) = -1.5708
    c: Tangent(g6,g5) = -1.5708
    c: Tangent(g7,g5) = 1.5708
    c: Vertical(g6)
    c: Symmetric(g0,g4,g-2)
    c: Symmetric(g1,g5,g-2)
    c: Equal(g0,g4)
    c: Diameter(g0) = 4
    c: DistanceY(g1,g0) = 3
    c: DistanceX(g0,g4) = 22
    c: DistanceY(g-1,g1) = 12
FEATURE [PartDesign::Pocket] Pocket067
  AllowMultiFace = false
  BaseFeature = -> Pocket062
  Length = 10
  Length2 = 100
  Profile = -> Sketch081
  Type = 0
FEATURE [PartDesign::Pocket] Pocket065
  AllowMultiFace = false
  BaseFeature = -> Pocket067
  Length = 11
  Length2 = 100
  Profile = -> Sketch076
  Type = 0
FEATURE [Sketcher::SketchObject] Sketch080
  MapMode = 5
  Placement = pos=(31,0,0) rot=(0.57735,0.57735,0.57735;2.0944rad)
  Support = -> [Pocket065]
  sketch-geometry (3):
    g0: LineSegment StartX=-31 StartY=11 StartZ=0 EndX=-31 EndY=9 EndZ=0
    g1: LineSegment StartX=-31 StartY=9 StartZ=0 EndX=-29 EndY=11 EndZ=0
    g2: LineSegment StartX=-29 StartY=11 StartZ=0 EndX=-31 EndY=11 EndZ=0
  constraints (9):
    c: Coincident(g0,g1)
    c: Coincident(g1,g2)
    c: Coincident(g2,g0)
    c: Vertical(g0)
    c: Horizontal(g2)
    c: DistanceX(g0,g1) = 2
    c: DistanceY(g0,g0) = 2
    c: DistanceX(g0,g-1) = 31
    c: DistanceY(g-1,g0) = 11
FEATURE [PartDesign::Pocket] Pocket066
  AllowMultiFace = false
  BaseFeature = -> Pocket065
  Length = 5
  Length2 = 100
  Profile = -> Sketch080
  Type = 1
FEATURE [PartDesign::Body] Body012  label="battery_adapter_einhell_x-change"
  Group = -> [Sketch072,Pad012,Sketch074,Pocket059,Sketch075,Pocket060,Sketch077,Pocket062,Pocket067,Sketch076,Pocket065,Sketch080,Pocket066,Sketch081]
  Origin = -> Origin122
  Placement = pos=(60,50,50) rot=(0,0,1;1.5708rad)
  Tip = -> Pocket066
COMPONENT P3 — recipe-attached ("top", modeled in this document).
Construction recipe (the document's own serialized feature program — sketch geometry with constraints, then the solid features built on it; lengths are millimeters unless a unit is written):

FEATURE [Sketcher::SketchObject] Sketch082
  MapMode = 5
  Support = -> [XY_Plane123]
  sketch-geometry (4):
    g0: LineSegment StartX=0 StartY=0 StartZ=0 EndX=130 EndY=0 EndZ=0
    g1: LineSegment StartX=130 StartY=0 StartZ=0 EndX=130 EndY=100 EndZ=0
    g2: LineSegment StartX=130 StartY=100 StartZ=0 EndX=0 EndY=100 EndZ=0
    g3: LineSegment StartX=0 StartY=100 StartZ=0 EndX=0 EndY=0 EndZ=0
  constraints (11):
    c: Coincident(g0,g1)
    c: Coincident(g1,g2)
    c: Coincident(g2,g3)
    c: Coincident(g3,g0)
    c: Horizontal(g0)
    c: Horizontal(g2)
    c: Vertical(g1)
    c: Vertical(g3)
    c: DistanceY(g1,g1) = 100
    c: DistanceX(g2,g2) = 130
    c: Coincident(g-1,g0)
FEATURE [PartDesign::Pad] Pad013  label="top001"
  AllowMultiFace = false
  Length = 5
  Length2 = 100
  Profile = -> Sketch082
  Type = 0
FEATURE [Sketcher::SketchObject] Sketch083
  MapMode = 5
  Placement = pos=(0,0,5) rot=(0,0,1;0rad)
  Support = -> [Pad013]
  sketch-geometry (4):
    g0: LineSegment StartX=10 StartY=81 StartZ=0 EndX=29 EndY=81 EndZ=0
    g1: LineSegment StartX=29 StartY=81 StartZ=0 EndX=29 EndY=19 EndZ=0
    g2: LineSegment StartX=29 StartY=19 StartZ=0 EndX=10 EndY=19 EndZ=0
    g3: LineSegment StartX=10 StartY=19 StartZ=0 EndX=10 EndY=81 EndZ=0
  constraints (10):
    c: Coincident(g0,g1)
    c: Coincident(g1,g2)
    c: Coincident(g2,g3)
    c: Coincident(g3,g0)
    c: Horizontal(g0)
    c: Horizontal(g2)
    c: Vertical(g1)
    c: Vertical(g3)
    c: DistanceX(g0,g0) = 19
    c: DistanceY(g1,g1) = 62
FEATURE [PartDesign::Pad] Pad014
  AllowMultiFace = false
  BaseFeature = -> Pad013
  Length = 18
  Length2 = 100
  Profile = -> Sketch083
  Type = 0
FEATURE [Sketcher::SketchObject] Sketch084
  MapMode = 5
  Placement = pos=(0,0,0) rot=(1,0,0;3.14159rad)
  Support = -> [Pad014]
  sketch-geometry (4):
    g0: LineSegment StartX=14 StartY=-25 StartZ=0 EndX=29 EndY=-25 EndZ=0
    g1: LineSegment StartX=29 StartY=-25 StartZ=0 EndX=29 EndY=-75 EndZ=0
    g2: LineSegment StartX=29 StartY=-75 StartZ=0 EndX=14 EndY=-75 EndZ=0
    g3: LineSegment StartX=14 StartY=-75 StartZ=0 EndX=14 EndY=-25 EndZ=0
  constraints (10):
    c: Coincident(g0,g1)
    c: Coincident(g1,g2)
    c: Coincident(g2,g3)
    c: Coincident(g3,g0)
    c: Horizontal(g0)
    c: Horizontal(g2)
    c: Vertical(g1)
    c: Vertical(g3)
    c: DistanceX(g2,g2) = 15
    c: DistanceY(g3,g3) = 50
FEATURE [PartDesign::Pocket] Pocket068
  AllowMultiFace = false
  BaseFeature = -> Pad014
  Length = 20
  Length2 = 100
  Profile = -> Sketch084
  Type = 0
FEATURE [Sketcher::SketchObject] Sketch085
  MapMode = 5
  Placement = pos=(0,0,0) rot=(1,0,0;3.14159rad)
  Support = -> [Pocket068]
  sketch-geometry (4):
    g0: Circle CenterX=5 CenterY=-5 CenterZ=0 NormalX=0 NormalY=0 NormalZ=1 AngleXU=0 Radius=1.5
    g1: Circle CenterX=125 CenterY=-5 CenterZ=0 NormalX=0 NormalY=0 NormalZ=1 AngleXU=0 Radius=1.5
    g2: Circle CenterX=5 CenterY=-95 CenterZ=0 NormalX=0 NormalY=0 NormalZ=1 AngleXU=0 Radius=1.5
    g3: Circle CenterX=125 CenterY=-95 CenterZ=0 NormalX=0 NormalY=0 NormalZ=1 AngleXU=0 Radius=1.5
  constraints (6):
    c: DistanceX(g0,g1) = 120
    c: DistanceY(g3,g1) = 90
    c: Equal(g0,g1)
    c: Equal(g1,g2)
    c: Equal(g2,g3)
    c: Radius(g0) = 1.5
FEATURE [PartDesign::Pocket] Pocket069
  AllowMultiFace = false
  BaseFeature = -> Pocket068
  Length = 5
  Length2 = 100
  Profile = -> Sketch085
  Type = 0
FEATURE [Sketcher::SketchObject] Sketch086
  MapMode = 5
  Placement = pos=(0,0,5) rot=(0,0,1;0rad)
  Support = -> [Pocket069]
  sketch-geometry (4):
    g0: Circle CenterX=5 CenterY=95 CenterZ=0 NormalX=0 NormalY=0 NormalZ=1 AngleXU=0 Radius=2.5
    g1: Circle CenterX=5 CenterY=5 CenterZ=0 NormalX=0 NormalY=0 NormalZ=1 AngleXU=0 Radius=2.5
    g2: Circle CenterX=125 CenterY=5 CenterZ=0 NormalX=0 NormalY=0 NormalZ=1 AngleXU=0 Radius=2.5
    g3: Circle CenterX=125 CenterY=95 CenterZ=0 NormalX=0 NormalY=0 NormalZ=1 AngleXU=0 Radius=2.5
  constraints (6):
    c: DistanceX(g0,g3) = 120
    c: DistanceY(g1,g0) = 90
    c: Equal(g0,g1)
    c: Equal(g1,g2)
    c: Equal(g1,g3)
    c: Radius(g0) = 2.5
FEATURE [PartDesign::Pocket] Pocket070
  AllowMultiFace = false
  BaseFeature = -> Pocket069
  Length = 2
  Length2 = 100
  Profile = -> Sketch086
  Type = 0
FEATURE [PartDesign::Body] Body013  label="top"
  Group = -> [Sketch082,Pad013,Sketch083,Pad014,Sketch084,Pocket068,Sketch085,Pocket069,Sketch086,Pocket070]
  Origin = -> Origin123
  Placement = pos=(0,0,45) rot=(0,0,1;0rad)
  Tip = -> Pocket070
COMPONENT P4 — recipe-attached ("spacer", modeled in this document).
Construction recipe (the document's own serialized feature program — sketch geometry with constraints, then the solid features built on it; lengths are millimeters unless a unit is written):

FEATURE [Sketcher::SketchObject] Sketch087
  MapMode = 5
  Support = -> [XY_Plane124]
  sketch-geometry (2):
    g0: Circle CenterX=10.4814 CenterY=8.40839 CenterZ=0 NormalX=0 NormalY=0 NormalZ=1 AngleXU=0 Radius=3
    g1: Circle CenterX=10.4814 CenterY=8.40839 CenterZ=0 NormalX=0 NormalY=0 NormalZ=1 AngleXU=0 Radius=1.6
  constraints (3):
    c: Coincident(g0,g1)
    c: Radius(g0) = 3
    c: Radius(g1) = 1.6
FEATURE [PartDesign::Pad] Pad015
  AllowMultiFace = false
  Length = 11
  Length2 = 100
  Profile = -> Sketch087
  Type = 0
FEATURE [PartDesign::Body] Body014  label="spacer"
  Group = -> [Sketch087,Pad015]
  Origin = -> Origin124
  Placement = pos=(0,0,10) rot=(0,0,1;0rad)
  Tip = -> Pad015
COMPONENT P5 — geometry summary ("ecu"; no construction recipe available for this part):
  bounding box: 100.0 x 60.0 x 2.9 mm
  tessellated surface: 8,632 triangles
  volume: 9458 mm^3 (54% of its bounding box)
  symmetry: 2-fold rotationally symmetric about the z axis; mirror-symmetric across its x mid-plane, y mid-plane
COMPONENT P6 — geometry summary ("highpowermotor"; no construction recipe available for this part):
  bounding box: 101.5 x 60.0 x 12.2 mm
  tessellated surface: 23,378 triangles
  volume: 12825 mm^3 (17% of its bounding box)
PROVENANCE & LICENSES
A FreeCAD (.FCStd) document from a public repository crawl; recipes are the document's own serialized feature recipes (and, for linked parts, companion documents' recipes).
License: as declared in the source repository (recorded in the dataset sidecar).
